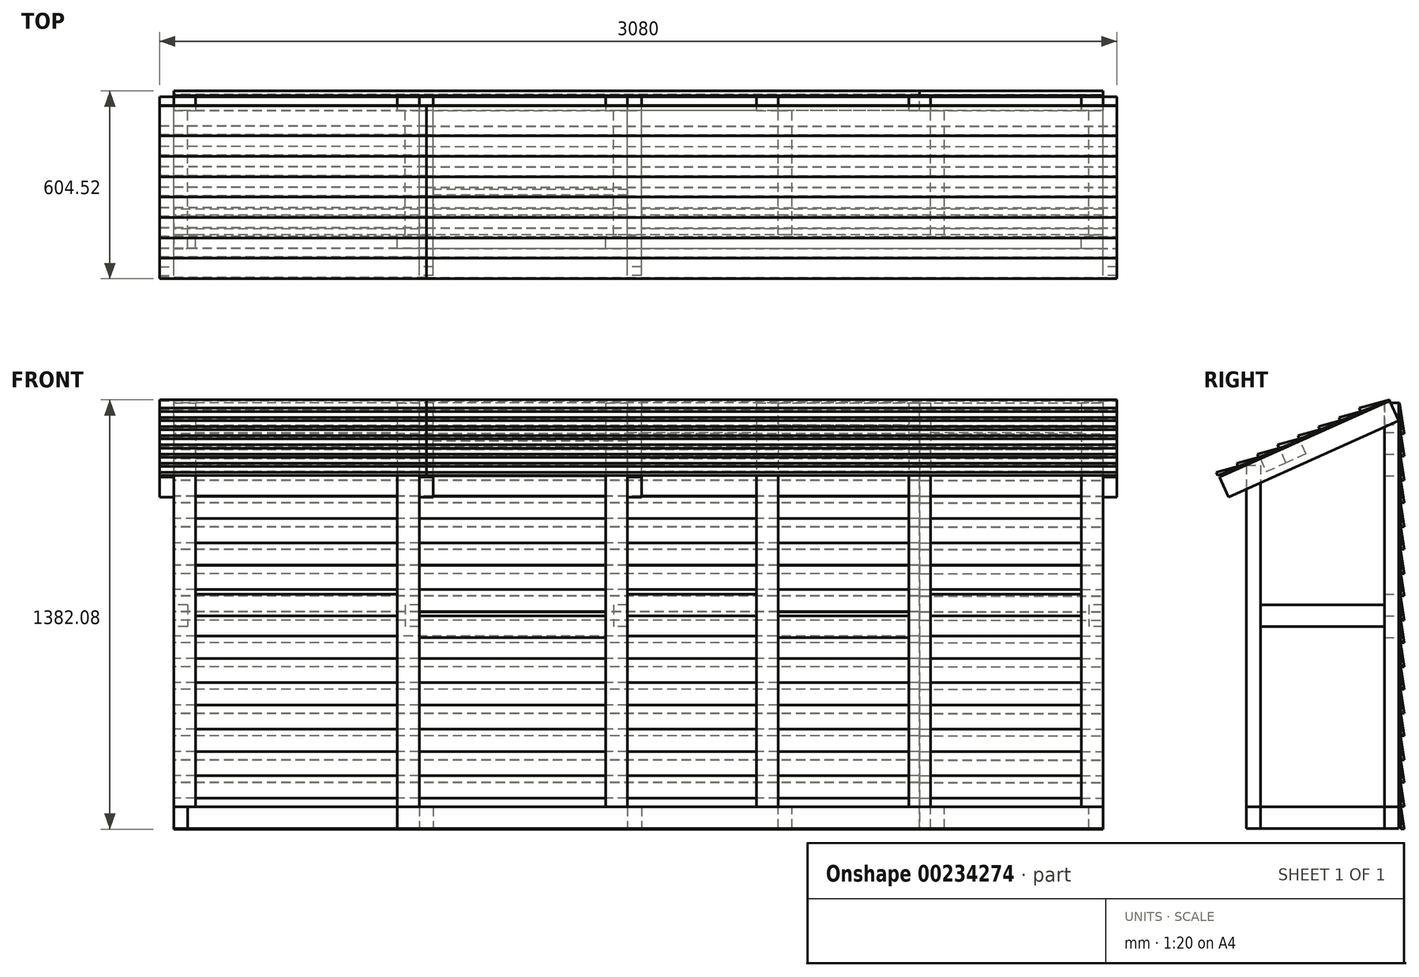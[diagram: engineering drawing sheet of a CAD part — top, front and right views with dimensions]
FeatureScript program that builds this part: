
annotation { "Feature Type Name" : "Feature", "Feature Type Description" : "" }
export const myFeature = defineFeature(function(context is Context, id is Id, definition is map)
    precondition{}
    {
        {
            var Q0;
            Q0=qCreatedBy(makeId("Top.planeOp"),FACE);
            cPlane(context, id + "F0", {"entities" : qUnion([Q0]), "cplaneType" : CPlaneType.OFFSET, "offset" : 70 * mm, "width" : 150 * mm, "height" : 150 * mm});
        }
        {
            var Q0;
            Q0=qCreatedBy(id+"F0.planeOp",FACE);
            var sketch = newSketch(context, id + "F1", { "sketchPlane" : qUnion([Q0])});
            skLineSegment(sketch, "E0.bottom", {"start": v(0, 0) * mm, "end": v(-70, 0) * mm});
            skLineSegment(sketch, "E0.top", {"start": v(0, -45) * mm, "end": v(-70, -45) * mm});
            skLineSegment(sketch, "E0.left", {"start": v(0, 0) * mm, "end": v(0, -45) * mm});
            skLineSegment(sketch, "E0.right", {"start": v(-70, 0) * mm, "end": v(-70, -45) * mm});
            skLineSegment(sketch, "E1.bottom", {"start": v(-2990, 0) * mm, "end": v(-2920, 0) * mm});
            skLineSegment(sketch, "E1.top", {"start": v(-2990, -45) * mm, "end": v(-2920, -45) * mm});
            skLineSegment(sketch, "E1.left", {"start": v(-2920, 0) * mm, "end": v(-2920, -45) * mm});
            skLineSegment(sketch, "E1.right", {"start": v(-2990, 0) * mm, "end": v(-2990, -45) * mm});
            skLineSegment(sketch, "E2.bottom", {"start": v(-2270, 0) * mm, "end": v(-2200, 0) * mm});
            skLineSegment(sketch, "E2.top", {"start": v(-2270, -45) * mm, "end": v(-2200, -45) * mm});
            skLineSegment(sketch, "E2.left", {"start": v(-2270, 0) * mm, "end": v(-2270, -45) * mm});
            skLineSegment(sketch, "E2.right", {"start": v(-2200, 0) * mm, "end": v(-2200, -45) * mm});
            skLineSegment(sketch, "E3.bottom", {"start": v(-1600, 0) * mm, "end": v(-1530, 0) * mm});
            skLineSegment(sketch, "E3.top", {"start": v(-1600, -45) * mm, "end": v(-1530, -45) * mm});
            skLineSegment(sketch, "E3.left", {"start": v(-1600, 0) * mm, "end": v(-1600, -45) * mm});
            skLineSegment(sketch, "E3.right", {"start": v(-1530, 0) * mm, "end": v(-1530, -45) * mm});
            skLineSegment(sketch, "E4.bottom", {"start": v(-1115, 0) * mm, "end": v(-1045, 0) * mm});
            skLineSegment(sketch, "E4.top", {"start": v(-1115, -45) * mm, "end": v(-1045, -45) * mm});
            skLineSegment(sketch, "E4.left", {"start": v(-1115, 0) * mm, "end": v(-1115, -45) * mm});
            skLineSegment(sketch, "E4.right", {"start": v(-1045, 0) * mm, "end": v(-1045, -45) * mm});
            skLineSegment(sketch, "E5.bottom", {"start": v(-625, 0) * mm, "end": v(-555, 0) * mm});
            skLineSegment(sketch, "E5.top", {"start": v(-625, -45) * mm, "end": v(-555, -45) * mm});
            skLineSegment(sketch, "E5.left", {"start": v(-625, 0) * mm, "end": v(-625, -45) * mm});
            skLineSegment(sketch, "E5.right", {"start": v(-555, 0) * mm, "end": v(-555, -45) * mm});
            skLineSegment(sketch, "E6.0.1.0", {"start": v(-1600, -445) * mm, "end": v(-1530, -445) * mm});
            skLineSegment(sketch, "E6.0.1.3", {"start": v(-2990, -445) * mm, "end": v(-2920, -445) * mm});
            skLineSegment(sketch, "E6.0.1.5", {"start": v(-2990, -445) * mm, "end": v(-2990, -490) * mm});
            skLineSegment(sketch, "E6.0.1.6", {"start": v(-70, -445) * mm, "end": v(-70, -490) * mm});
            skLineSegment(sketch, "E6.0.1.7", {"start": v(-2990, -490) * mm, "end": v(-2920, -490) * mm});
            skLineSegment(sketch, "E6.0.1.8", {"start": v(-2920, -445) * mm, "end": v(-2920, -490) * mm});
            skLineSegment(sketch, "E6.0.1.9", {"start": v(-2270, -490) * mm, "end": v(-2200, -490) * mm});
            skLineSegment(sketch, "E6.0.1.11", {"start": v(0, -445) * mm, "end": v(0, -490) * mm});
            skLineSegment(sketch, "E6.0.1.12", {"start": v(-1600, -490) * mm, "end": v(-1530, -490) * mm});
            skLineSegment(sketch, "E6.0.1.13", {"start": v(-1600, -445) * mm, "end": v(-1600, -490) * mm});
            skLineSegment(sketch, "E6.0.1.14", {"start": v(-1530, -445) * mm, "end": v(-1530, -490) * mm});
            skLineSegment(sketch, "E6.0.1.15", {"start": v(0, -445) * mm, "end": v(-70, -445) * mm});
            skLineSegment(sketch, "E6.0.1.16", {"start": v(0, -490) * mm, "end": v(-70, -490) * mm});
            skLineSegment(sketch, "E6.0.1.20", {"start": v(-2200, -445) * mm, "end": v(-2200, -490) * mm});
            skLineSegment(sketch, "E6.0.1.21", {"start": v(-2270, -445) * mm, "end": v(-2270, -490) * mm});
            skLineSegment(sketch, "E6.0.1.23", {"start": v(-2270, -445) * mm, "end": v(-2200, -445) * mm});
            skLineSegment(sketch, "E6.direction1", {"start": v(-2990, -45) * mm, "end": v(-2875, -45) * mm, "construction": true});
            skLineSegment(sketch, "E6.direction2", {"start": v(-2990, -45) * mm, "end": v(-2990, -490) * mm, "construction": true});
            skSolve(sketch);
        }
        {
            var Q0;
            Q0=qSketchRegion(id+"F1",true);
            extrude(context, id + "F2", {"entities" : qUnion([Q0]), "depth" : 1300 * mm});
        }
        {
            var Q0;
            Q0=makeQuery(id+"F2.opExtrude","SWEPT_FACE",FACE,{"disambiguationData":[OSD([sQuery(id+"F1.wireOp",EDGE,"E0.top")])]});
            var sketch = newSketch(context, id + "F3", { "sketchPlane" : qUnion([Q0])});
            skLineSegment(sketch, "E7.bottom", {"start": v(-2920, 0) * mm, "end": v(-2875, 0) * mm, "construction": true});
            skLineSegment(sketch, "E7.top", {"start": v(-2920, 70) * mm, "end": v(-2875, 70) * mm, "construction": true});
            skLineSegment(sketch, "E7.left", {"start": v(-2920, 0) * mm, "end": v(-2920, 70) * mm, "construction": true});
            skLineSegment(sketch, "E7.right", {"start": v(-2875, 0) * mm, "end": v(-2875, 70) * mm, "construction": true});
            skLineSegment(sketch, "E8.bottom", {"start": v(-45, 0) * mm, "end": v(0, 0) * mm});
            skLineSegment(sketch, "E8.top", {"start": v(-45, 70) * mm, "end": v(0, 70) * mm});
            skLineSegment(sketch, "E8.left", {"start": v(-45, 0) * mm, "end": v(-45, 70) * mm});
            skLineSegment(sketch, "E8.right", {"start": v(0, 0) * mm, "end": v(0, 70) * mm});
            skLineSegment(sketch, "E9.0.1.0", {"start": v(-2990, 715) * mm, "end": v(-2920, 715) * mm});
            skLineSegment(sketch, "E9.0.1.2", {"start": v(-2990, 670) * mm, "end": v(-2990, 715) * mm});
            skLineSegment(sketch, "E9.0.1.5", {"start": v(-2990, 670) * mm, "end": v(-2920, 670) * mm});
            skLineSegment(sketch, "E9.0.1.7", {"start": v(-2920, 670) * mm, "end": v(-2920, 715) * mm});
            skLineSegment(sketch, "E9.0.1.9", {"start": v(-2200, 670) * mm, "end": v(-2200, 715) * mm});
            skLineSegment(sketch, "E9.0.1.10", {"start": v(-1600, 670) * mm, "end": v(-1530, 670) * mm});
            skLineSegment(sketch, "E9.0.1.11", {"start": v(-2270, 670) * mm, "end": v(-2200, 670) * mm});
            skLineSegment(sketch, "E9.0.1.12", {"start": v(-2270, 670) * mm, "end": v(-2270, 715) * mm});
            skLineSegment(sketch, "E9.0.1.13", {"start": v(-2270, 715) * mm, "end": v(-2200, 715) * mm});
            skLineSegment(sketch, "E9.0.1.14", {"start": v(-1600, 670) * mm, "end": v(-1600, 715) * mm});
            skLineSegment(sketch, "E9.0.1.15", {"start": v(-1530, 670) * mm, "end": v(-1530, 715) * mm});
            skLineSegment(sketch, "E9.0.1.16", {"start": v(-1600, 715) * mm, "end": v(-1530, 715) * mm});
            skLineSegment(sketch, "E9.0.1.17", {"start": v(-70, 670) * mm, "end": v(-70, 715) * mm});
            skLineSegment(sketch, "E9.0.1.18", {"start": v(-70, 670) * mm, "end": v(0, 670) * mm});
            skLineSegment(sketch, "E9.0.1.19", {"start": v(0, 670) * mm, "end": v(0, 715) * mm});
            skLineSegment(sketch, "E9.0.1.20", {"start": v(-70, 715) * mm, "end": v(0, 715) * mm});
            skLineSegment(sketch, "E10.bottom", {"start": v(-2200, 70) * mm, "end": v(-2155, 70) * mm});
            skLineSegment(sketch, "E10.top", {"start": v(-2200, 0) * mm, "end": v(-2155, 0) * mm});
            skLineSegment(sketch, "E10.left", {"start": v(-2200, 70) * mm, "end": v(-2200, 0) * mm});
            skLineSegment(sketch, "E10.right", {"start": v(-2155, 70) * mm, "end": v(-2155, 0) * mm});
            skLineSegment(sketch, "E11.bottom", {"start": v(-1530, 70) * mm, "end": v(-1485, 70) * mm});
            skLineSegment(sketch, "E11.top", {"start": v(-1530, 0) * mm, "end": v(-1485, 0) * mm});
            skLineSegment(sketch, "E11.left", {"start": v(-1530, 70) * mm, "end": v(-1530, 0) * mm});
            skLineSegment(sketch, "E11.right", {"start": v(-1485, 70) * mm, "end": v(-1485, 0) * mm});
            skSolve(sketch);
        }
        {
            var Q0;
            Q0=makeQuery(id+"F3.imprint","IMPRINT",FACE,{"disambiguationData":[TD([[makeQuery(id+"F3.imprint","IMPRINT",EDGE,{"derivedFrom":sQuery(id+"F3.wireOp",EDGE,"E8.bottom")}),1.0]])]});
            var Q1;
            Q1=makeQuery(id+"F3.imprint","IMPRINT",FACE,{"disambiguationData":[TD([[makeQuery(id+"F3.imprint","IMPRINT",EDGE,{"derivedFrom":sQuery(id+"F3.wireOp",EDGE,"E11.bottom")}),-1.0]])]});
            var Q2;
            Q2=makeQuery(id+"F3.imprint","IMPRINT",FACE,{"disambiguationData":[TD([[makeQuery(id+"F3.imprint","IMPRINT",EDGE,{"derivedFrom":sQuery(id+"F3.wireOp",EDGE,"E10.bottom")}),-1.0]])]});
            var Q3;
            Q3=makeQuery(id+"F3.imprint","IMPRINT",FACE,{"disambiguationData":[TD([[makeQuery(id+"F3.imprint","IMPRINT",EDGE,{"derivedFrom":sQuery(id+"F3.wireOp",EDGE,"E7.bottom")}),1.0]])]});
            var Q4;
            Q4=makeQuery(id+"F2.opExtrude","SWEPT_FACE",FACE,{"disambiguationData":[OSD([sQuery(id+"F1.wireOp",EDGE,"E6.0.1.15")])]});
            extrude(context, id + "F4", {"entities" : qUnion([Q0, Q1, Q2, Q3]), "endBound" : BoundingType.UP_TO_SURFACE, "endBoundEntityFace" : qUnion([Q4]), "depth" : 25 * mm});
        }
        {
            var Q0;
            Q0=makeQuery(id+"F2.opExtrude","SWEPT_FACE",FACE,{"disambiguationData":[OSD([sQuery(id+"F1.wireOp",EDGE,"E1.right")])]});
            var sketch = newSketch(context, id + "F5", { "sketchPlane" : qUnion([Q0])});
            skLineSegment(sketch, "E12.0", {"start": v(45, 0) * mm, "end": v(0, 0) * mm});
            skLineSegment(sketch, "E12.1", {"start": v(45, 70) * mm, "end": v(0, 70) * mm});
            skLineSegment(sketch, "E12.3", {"start": v(0, 0) * mm, "end": v(0, 70) * mm});
            skLineSegment(sketch, "E13", {"start": v(45, 70) * mm, "end": v(45, 0) * mm});
            skSolve(sketch);
        }
        {
            var Q0;
            Q0=qSketchRegion(id+"F5",true);
            var Q1;
            Q1=makeQuery(id+"F4.opExtrude","SWEPT_FACE",FACE,{"disambiguationData":[OSD([sQuery(id+"F3.wireOp",EDGE,"E11.left")])]});
            extrude(context, id + "F6", {"entities" : qUnion([Q0]), "oppositeDirection" : true, "endBoundEntityFace" : qUnion([Q1]), "depth" : 2400 * mm});
        }
        {
            var Q0;
            Q0=makeQuery(id+"F2.opExtrude","SWEPT_FACE",FACE,{"disambiguationData":[OSD([sQuery(id+"F1.wireOp",EDGE,"E0.left")])]});
            var sketch = newSketch(context, id + "F7", { "sketchPlane" : qUnion([Q0])});
            skLineSegment(sketch, "E14.bottom", {"start": v(-45, 0) * mm, "end": v(0, 0) * mm});
            skLineSegment(sketch, "E14.top", {"start": v(-45, 70) * mm, "end": v(0, 70) * mm});
            skLineSegment(sketch, "E14.right", {"start": v(0, 0) * mm, "end": v(0, 70) * mm});
            skLineSegment(sketch, "E15", {"start": v(-45, 70) * mm, "end": v(-45, 0) * mm});
            skSolve(sketch);
        }
        {
            var Q0;
            Q0=makeQuery(id+"F2.opExtrude","SWEPT_FACE",FACE,{"disambiguationData":[OSD([sQuery(id+"F1.wireOp",EDGE,"E1.right")])]});
            var sketch = newSketch(context, id + "F8", { "sketchPlane" : qUnion([Q0])});
            skLineSegment(sketch, "E16", {"start": v(490, 1170) * mm, "end": v(490, 1370) * mm});
            skLineSegment(sketch, "E17", {"start": v(490, 1370) * mm, "end": v(445, 1370) * mm});
            skPoint(sketch, "E18", {"position": v(445, 1170) * mm});
            skLineSegment(sketch, "E19", {"start": v(445, 1170) * mm, "end": v(445, 1370) * mm});
            skLineSegment(sketch, "E20", {"start": v(445, 1170) * mm, "end": v(490, 1170) * mm});
            skSolve(sketch);
        }
        {
            var Q0;
            Q0=qSketchRegion(id+"F8",true);
            extrude(context, id + "F9", {"entities" : qUnion([Q0]), "operationType" : NewBodyOperationType.REMOVE, "endBound" : BoundingType.THROUGH_ALL, "oppositeDirection" : true, "depth" : 25 * mm});
        }
        {
            var Q0;
            Q0=makeQuery(id+"F2.opExtrude","SWEPT_FACE",FACE,{"disambiguationData":[OSD([sQuery(id+"F1.wireOp",EDGE,"E6.0.1.21")])]});
            var sketch = newSketch(context, id + "F10", { "sketchPlane" : qUnion([Q0])});
            skLineSegment(sketch, "E21.bottom", {"start": v(490, 70) * mm, "end": v(445, 70) * mm});
            skLineSegment(sketch, "E21.top", {"start": v(490, 0) * mm, "end": v(445, 0) * mm});
            skLineSegment(sketch, "E21.left", {"start": v(490, 70) * mm, "end": v(490, 0) * mm});
            skLineSegment(sketch, "E22", {"start": v(445, 70) * mm, "end": v(445, 0) * mm});
            skPoint(sketch, "E23.orphan", {"position": v(445, 0) * mm});
            skSolve(sketch);
        }
        {
            var Q0;
            Q0=qSketchRegion(id+"F10",true);
            var Q1;
            Q1=makeQuery(id+"F2.opExtrude","SWEPT_FACE",FACE,{"disambiguationData":[OSD([sQuery(id+"F1.wireOp",EDGE,"E6.0.1.11")])]});
            extrude(context, id + "F11", {"entities" : qUnion([Q0]), "endBound" : BoundingType.UP_TO_SURFACE, "oppositeDirection" : true, "endBoundEntityFace" : qUnion([Q1]), "depth" : 25 * mm});
        }
        {
            var Q0;
            Q0=makeQuery(id+"F2.opExtrude","SWEPT_FACE",FACE,{"disambiguationData":[OSD([sQuery(id+"F1.wireOp",EDGE,"E3.right")])]});
            var sketch = newSketch(context, id + "F12", { "sketchPlane" : qUnion([Q0])});
            skLineSegment(sketch, "E24.bottom", {"start": v(-45, 755) * mm, "end": v(0, 755) * mm});
            skLineSegment(sketch, "E24.top", {"start": v(-45, 685) * mm, "end": v(0, 685) * mm});
            skLineSegment(sketch, "E24.left", {"start": v(-45, 755) * mm, "end": v(-45, 685) * mm});
            skLineSegment(sketch, "E24.right", {"start": v(0, 755) * mm, "end": v(0, 685) * mm});
            skSolve(sketch);
        }
        {
            var Q0;
            Q0=qSketchRegion(id+"F12",true);
            extrude(context, id + "F13", {"entities" : qUnion([Q0]), "endBound" : BoundingType.UP_TO_NEXT, "depth" : 25 * mm});
        }
        {
            var Q0;
            Q0=makeQuery(id+"F2.opExtrude","SWEPT_FACE",FACE,{"disambiguationData":[OSD([sQuery(id+"F1.wireOp",EDGE,"E5.right")])]});
            var sketch = newSketch(context, id + "F14", { "sketchPlane" : qUnion([Q0])});
            skLineSegment(sketch, "E25.0", {"start": v(-45, 755) * mm, "end": v(0, 755) * mm});
            skLineSegment(sketch, "E25.1", {"start": v(-45, 685) * mm, "end": v(0, 685) * mm});
            skLineSegment(sketch, "E25.2", {"start": v(-45, 755) * mm, "end": v(-45, 685) * mm});
            skLineSegment(sketch, "E25.3", {"start": v(0, 755) * mm, "end": v(0, 685) * mm});
            skSolve(sketch);
        }
        {
            var Q0;
            Q0=qSketchRegion(id+"F14",true);
            extrude(context, id + "F15", {"entities" : qUnion([Q0]), "endBound" : BoundingType.UP_TO_NEXT, "depth" : 25 * mm});
        }
        {
            var Q0;
            Q0=makeQuery(id+"F2.opExtrude","SWEPT_FACE",FACE,{"disambiguationData":[OSD([sQuery(id+"F1.wireOp",EDGE,"E4.right")])]});
            var sketch = newSketch(context, id + "F16", { "sketchPlane" : qUnion([Q0])});
            skPoint(sketch, "E26.firstSnap0", {"position": v(0, 685) * mm});
            skLineSegment(sketch, "E26.bottom", {"start": v(-45, 685) * mm, "end": v(0, 685) * mm});
            skLineSegment(sketch, "E26.top", {"start": v(-45, 615) * mm, "end": v(0, 615) * mm});
            skLineSegment(sketch, "E26.left", {"start": v(-45, 685) * mm, "end": v(-45, 615) * mm});
            skLineSegment(sketch, "E26.right", {"start": v(0, 685) * mm, "end": v(0, 615) * mm});
            skSolve(sketch);
        }
        {
            var Q0;
            Q0=qSketchRegion(id+"F16",true);
            extrude(context, id + "F17", {"entities" : qUnion([Q0]), "endBound" : BoundingType.UP_TO_NEXT, "depth" : 25 * mm});
        }
        {
            var Q0;
            Q0=makeQuery(id+"F2.opExtrude","SWEPT_FACE",FACE,{"disambiguationData":[OSD([sQuery(id+"F1.wireOp",EDGE,"E3.left")])]});
            var sketch = newSketch(context, id + "F18", { "sketchPlane" : qUnion([Q0])});
            skLineSegment(sketch, "E27.top", {"start": v(45, 685) * mm, "end": v(0, 685) * mm});
            skLineSegment(sketch, "E27.left", {"start": v(45, 615) * mm, "end": v(45, 685) * mm});
            skLineSegment(sketch, "E27.right", {"start": v(0, 615) * mm, "end": v(0, 685) * mm});
            skLineSegment(sketch, "E28", {"start": v(0, 615) * mm, "end": v(45, 615) * mm});
            skSolve(sketch);
        }
        {
            var Q0;
            Q0=qSketchRegion(id+"F18",true);
            extrude(context, id + "F19", {"entities" : qUnion([Q0]), "endBound" : BoundingType.UP_TO_NEXT, "depth" : 25 * mm});
        }
        {
            var Q0;
            Q0=makeQuery(id+"F2.opExtrude","SWEPT_FACE",FACE,{"disambiguationData":[OSD([sQuery(id+"F1.wireOp",EDGE,"E2.left")])]});
            var sketch = newSketch(context, id + "F20", { "sketchPlane" : qUnion([Q0])});
            skLineSegment(sketch, "E29.0", {"start": v(45, 755) * mm, "end": v(0, 755) * mm});
            skLineSegment(sketch, "E29.1", {"start": v(45, 685) * mm, "end": v(0, 685) * mm});
            skLineSegment(sketch, "E29.2", {"start": v(45, 755) * mm, "end": v(45, 685) * mm});
            skLineSegment(sketch, "E29.3", {"start": v(0, 755) * mm, "end": v(0, 685) * mm});
            skSolve(sketch);
        }
        {
            var Q0;
            Q0=qSketchRegion(id+"F20",true);
            extrude(context, id + "F21", {"entities" : qUnion([Q0]), "endBound" : BoundingType.UP_TO_NEXT, "depth" : 25 * mm});
        }
        {
            var Q0;
            Q0=makeQuery(id+"F2.opExtrude","SWEPT_FACE",FACE,{"disambiguationData":[OSD([sQuery(id+"F1.wireOp",EDGE,"E0.left")])]});
            var sketch = newSketch(context, id + "F22", { "sketchPlane" : qUnion([Q0])});
            skLineSegment(sketch, "E30", {"start": v(-575.96, 1131.36) * mm, "end": v(-28.7, 1377.33) * mm});
            skLineSegment(sketch, "E31", {"start": v(-575.96, 1131.36) * mm, "end": v(-547.27, 1067.52) * mm});
            skLineSegment(sketch, "E32", {"start": v(-547.27, 1067.52) * mm, "end": v(0, 1313.48) * mm});
            skLineSegment(sketch, "E33", {"start": v(-28.7, 1377.33) * mm, "end": v(0, 1313.48) * mm});
            skSolve(sketch);
        }
        {
            var Q0;
            Q0=qSketchRegion(id+"F22",true);
            extrude(context, id + "F23", {"entities" : qUnion([Q0]), "depth" : 45 * mm});
        }
        {
            var Q0;
            Q0=makeQuery(id+"F2.opExtrude","SWEPT_FACE",FACE,{"disambiguationData":[OSD([sQuery(id+"F1.wireOp",EDGE,"E6.0.1.5")])]});
            var sketch = newSketch(context, id + "F24", { "sketchPlane" : qUnion([Q0])});
            skLineSegment(sketch, "E34.0", {"start": v(575.96, 1131.36) * mm, "end": v(28.7, 1377.33) * mm});
            skLineSegment(sketch, "E34.1", {"start": v(575.96, 1131.36) * mm, "end": v(547.27, 1067.52) * mm});
            skLineSegment(sketch, "E34.2", {"start": v(547.27, 1067.52) * mm, "end": v(0, 1313.48) * mm});
            skLineSegment(sketch, "E34.3", {"start": v(28.7, 1377.33) * mm, "end": v(0, 1313.48) * mm});
            skSolve(sketch);
        }
        {
            var Q0;
            Q0=qSketchRegion(id+"F24",true);
            extrude(context, id + "F25", {"entities" : qUnion([Q0]), "depth" : 45 * mm});
        }
        {
            var Q0;
            Q0=makeQuery(id+"F2.opExtrude","SWEPT_FACE",FACE,{"disambiguationData":[OSD([sQuery(id+"F1.wireOp",EDGE,"E6.0.1.14")])]});
            var sketch = newSketch(context, id + "F26", { "sketchPlane" : qUnion([Q0])});
            skLineSegment(sketch, "E35.0", {"start": v(-575.96, 1131.36) * mm, "end": v(-28.7, 1377.33) * mm});
            skLineSegment(sketch, "E35.1", {"start": v(-575.96, 1131.36) * mm, "end": v(-547.27, 1067.52) * mm});
            skLineSegment(sketch, "E35.2", {"start": v(-547.27, 1067.52) * mm, "end": v(0, 1313.48) * mm});
            skLineSegment(sketch, "E35.3", {"start": v(-28.7, 1377.33) * mm, "end": v(0, 1313.48) * mm});
            skSolve(sketch);
        }
        {
            var Q0;
            Q0=qSketchRegion(id+"F26",true);
            extrude(context, id + "F27", {"entities" : qUnion([Q0]), "depth" : 45 * mm});
        }
        {
            var Q0;
            Q0=makeQuery(id+"F2.opExtrude","SWEPT_FACE",FACE,{"disambiguationData":[OSD([sQuery(id+"F1.wireOp",EDGE,"E2.right")])]});
            var sketch = newSketch(context, id + "F28", { "sketchPlane" : qUnion([Q0])});
            skLineSegment(sketch, "E36.0", {"start": v(-575.96, 1131.36) * mm, "end": v(-28.7, 1377.33) * mm});
            skLineSegment(sketch, "E36.1", {"start": v(-575.96, 1131.36) * mm, "end": v(-547.27, 1067.52) * mm});
            skLineSegment(sketch, "E36.2", {"start": v(-547.27, 1067.52) * mm, "end": v(0, 1313.48) * mm});
            skLineSegment(sketch, "E36.3", {"start": v(-28.7, 1377.33) * mm, "end": v(0, 1313.48) * mm});
            skSolve(sketch);
        }
        {
            var Q0;
            Q0=qSketchRegion(id+"F28",true);
            extrude(context, id + "F29", {"entities" : qUnion([Q0]), "depth" : 45 * mm});
        }
        {
            var Q0;
            Q0=makeQuery(id+"F25.opExtrude","CAP_FACE",FACE,{"disambiguationData":[OSD([sQuery(id+"F24.wireOp",EDGE,"E34.0"),sQuery(id+"F24.wireOp",EDGE,"E34.1"),sQuery(id+"F24.wireOp",EDGE,"E34.2"),sQuery(id+"F24.wireOp",EDGE,"E34.3")])],"isStart":true});
            var sketch = newSketch(context, id + "F30", { "sketchPlane" : qUnion([Q0])});
            skLineSegment(sketch, "E37", {"start": v(-445, 1190.22) * mm, "end": v(-426.55, 1149.18) * mm});
            skLineSegment(sketch, "E38", {"start": v(-362.7, 1177.88) * mm, "end": v(-381.15, 1218.92) * mm});
            skLineSegment(sketch, "E39", {"start": v(-381.15, 1218.92) * mm, "end": v(-445, 1190.22) * mm});
            skLineSegment(sketch, "E40", {"start": v(-362.7, 1177.88) * mm, "end": v(-426.55, 1149.18) * mm});
            skSolve(sketch);
        }
        {
            var Q0;
            Q0=qSketchRegion(id+"F30",true);
            extrude(context, id + "F31", {"entities" : qUnion([Q0]), "endBound" : BoundingType.UP_TO_NEXT, "depth" : 25 * mm});
        }
        {
            var Q0;
            Q0=makeQuery(id+"F29.opExtrude","CAP_FACE",FACE,{"disambiguationData":[OSD([sQuery(id+"F28.wireOp",EDGE,"E36.0"),sQuery(id+"F28.wireOp",EDGE,"E36.1"),sQuery(id+"F28.wireOp",EDGE,"E36.2"),sQuery(id+"F28.wireOp",EDGE,"E36.3")])],"isStart":false});
            var sketch = newSketch(context, id + "F32", { "sketchPlane" : qUnion([Q0])});
            skLineSegment(sketch, "E41", {"start": v(-317.3, 1247.62) * mm, "end": v(-381.15, 1218.92) * mm});
            skLineSegment(sketch, "E42", {"start": v(-381.15, 1218.92) * mm, "end": v(-362.7, 1177.88) * mm});
            skLineSegment(sketch, "E43", {"start": v(-298.86, 1206.57) * mm, "end": v(-317.3, 1247.62) * mm});
            skLineSegment(sketch, "E44", {"start": v(-298.86, 1206.57) * mm, "end": v(-362.7, 1177.88) * mm});
            skSolve(sketch);
        }
        {
            var Q0;
            Q0=qSketchRegion(id+"F32",true);
            extrude(context, id + "F33", {"entities" : qUnion([Q0]), "endBound" : BoundingType.UP_TO_NEXT, "depth" : 25 * mm});
        }
        {
            var Q0;
            Q0=makeQuery(id+"F2.opExtrude","SWEPT_FACE",FACE,{"disambiguationData":[OSD([sQuery(id+"F1.wireOp",EDGE,"E0.right")])]});
            var sketch = newSketch(context, id + "F34", { "sketchPlane" : qUnion([Q0])});
            skLineSegment(sketch, "E45.bottom", {"start": v(0, 1275) * mm, "end": v(45, 1275) * mm});
            skLineSegment(sketch, "E45.top", {"start": v(0, 1205) * mm, "end": v(45, 1205) * mm});
            skLineSegment(sketch, "E45.left", {"start": v(0, 1275) * mm, "end": v(0, 1205) * mm});
            skLineSegment(sketch, "E45.right", {"start": v(45, 1275) * mm, "end": v(45, 1205) * mm});
            skLineSegment(sketch, "E46", {"start": v(0, 1240) * mm, "end": v(45, 1240) * mm, "construction": true});
            skSolve(sketch);
        }
        {
            var Q0;
            Q0=qSketchRegion(id+"F34",true);
            extrude(context, id + "F35", {"entities" : qUnion([Q0]), "endBound" : BoundingType.UP_TO_NEXT, "depth" : 25 * mm});
        }
        {
            var Q0;
            Q0=makeQuery(id+"F2.opExtrude","SWEPT_FACE",FACE,{"disambiguationData":[OSD([sQuery(id+"F1.wireOp",EDGE,"E5.left")])]});
            var sketch = newSketch(context, id + "F36", { "sketchPlane" : qUnion([Q0])});
            skLineSegment(sketch, "E47.bottom", {"start": v(0, 1370) * mm, "end": v(45, 1370) * mm});
            skLineSegment(sketch, "E47.top", {"start": v(0, 1300) * mm, "end": v(45, 1300) * mm});
            skLineSegment(sketch, "E47.left", {"start": v(0, 1370) * mm, "end": v(0, 1300) * mm});
            skLineSegment(sketch, "E47.right", {"start": v(45, 1370) * mm, "end": v(45, 1300) * mm});
            skSolve(sketch);
        }
        {
            var Q0;
            Q0=qSketchRegion(id+"F36",true);
            extrude(context, id + "F37", {"entities" : qUnion([Q0]), "endBound" : BoundingType.UP_TO_NEXT, "depth" : 25 * mm});
        }
        {
            var Q0;
            Q0=makeQuery(id+"F2.opExtrude","SWEPT_FACE",FACE,{"disambiguationData":[OSD([sQuery(id+"F1.wireOp",EDGE,"E4.left")])]});
            var sketch = newSketch(context, id + "F38", { "sketchPlane" : qUnion([Q0])});
            skLineSegment(sketch, "E48.0", {"start": v(0, 1275) * mm, "end": v(45, 1275) * mm});
            skLineSegment(sketch, "E48.1", {"start": v(0, 1205) * mm, "end": v(45, 1205) * mm});
            skLineSegment(sketch, "E48.2", {"start": v(0, 1275) * mm, "end": v(0, 1205) * mm});
            skLineSegment(sketch, "E48.3", {"start": v(45, 1275) * mm, "end": v(45, 1205) * mm});
            skSolve(sketch);
        }
        {
            var Q0;
            Q0=qSketchRegion(id+"F38",true);
            extrude(context, id + "F39", {"entities" : qUnion([Q0]), "endBound" : BoundingType.UP_TO_NEXT, "depth" : 25 * mm});
        }
        {
            var Q0;
            Q0=makeQuery(id+"F2.opExtrude","SWEPT_FACE",FACE,{"disambiguationData":[OSD([sQuery(id+"F1.wireOp",EDGE,"E3.left")])]});
            var sketch = newSketch(context, id + "F40", { "sketchPlane" : qUnion([Q0])});
            skLineSegment(sketch, "E49.bottom", {"start": v(0, 1205) * mm, "end": v(45, 1205) * mm});
            skLineSegment(sketch, "E49.top", {"start": v(0, 1135) * mm, "end": v(45, 1135) * mm});
            skLineSegment(sketch, "E49.left", {"start": v(0, 1205) * mm, "end": v(0, 1135) * mm});
            skLineSegment(sketch, "E49.right", {"start": v(45, 1205) * mm, "end": v(45, 1135) * mm});
            skSolve(sketch);
        }
        {
            var Q0;
            Q0=qSketchRegion(id+"F40",true);
            extrude(context, id + "F41", {"entities" : qUnion([Q0]), "endBound" : BoundingType.UP_TO_NEXT, "depth" : 25 * mm});
        }
        {
            var Q0;
            Q0=makeQuery(id+"F2.opExtrude","SWEPT_FACE",FACE,{"disambiguationData":[OSD([sQuery(id+"F1.wireOp",EDGE,"E2.left")])]});
            var sketch = newSketch(context, id + "F42", { "sketchPlane" : qUnion([Q0])});
            skLineSegment(sketch, "E50.bottom", {"start": v(0, 1205) * mm, "end": v(45, 1205) * mm});
            skLineSegment(sketch, "E50.top", {"start": v(0, 1275) * mm, "end": v(45, 1275) * mm});
            skLineSegment(sketch, "E50.left", {"start": v(0, 1205) * mm, "end": v(0, 1275) * mm});
            skLineSegment(sketch, "E50.right", {"start": v(45, 1205) * mm, "end": v(45, 1275) * mm});
            skSolve(sketch);
        }
        {
            var Q0;
            Q0=qSketchRegion(id+"F42",true);
            extrude(context, id + "F43", {"entities" : qUnion([Q0]), "endBound" : BoundingType.UP_TO_NEXT, "depth" : 25 * mm});
        }
        {
            var Q0;
            Q0=makeQuery(id+"F27.opExtrude","CAP_FACE",FACE,{"disambiguationData":[OSD([sQuery(id+"F26.wireOp",EDGE,"E35.0"),sQuery(id+"F26.wireOp",EDGE,"E35.1"),sQuery(id+"F26.wireOp",EDGE,"E35.2"),sQuery(id+"F26.wireOp",EDGE,"E35.3")])],"isStart":false});
            var sketch = newSketch(context, id + "F44", { "sketchPlane" : qUnion([Q0])});
            skLineSegment(sketch, "E51.0.1", {"start": v(-445, 1190.22) * mm, "end": v(-381.15, 1218.92) * mm});
            skLineSegment(sketch, "E51.0.3", {"start": v(-381.15, 1218.92) * mm, "end": v(-445, 1190.22) * mm});
            skLineSegment(sketch, "E51.1", {"start": v(-445, 1190.22) * mm, "end": v(-426.55, 1149.18) * mm});
            skLineSegment(sketch, "E51.3", {"start": v(-362.7, 1177.88) * mm, "end": v(-381.15, 1218.92) * mm});
            skLineSegment(sketch, "E51.4", {"start": v(-381.15, 1218.92) * mm, "end": v(-445, 1190.22) * mm});
            skLineSegment(sketch, "E52", {"start": v(-426.55, 1149.18) * mm, "end": v(-362.7, 1177.88) * mm});
            skSolve(sketch);
        }
        {
            var Q0;
            Q0=qSketchRegion(id+"F44",true);
            extrude(context, id + "F45", {"entities" : qUnion([Q0]), "endBound" : BoundingType.UP_TO_NEXT, "depth" : 25 * mm});
        }
        {
            var Q0;
            Q0=makeQuery(id+"F2.opExtrude","SWEPT_FACE",FACE,{"disambiguationData":[OSD([sQuery(id+"F1.wireOp",EDGE,"E1.right")])]});
            var sketch = newSketch(context, id + "F46", { "sketchPlane" : qUnion([Q0])});
            skLineSegment(sketch, "E53", {"start": v(0, 1370) * mm, "end": v(-7.26, 1270.26) * mm});
            skLineSegment(sketch, "E54", {"start": v(-7.26, 1270.26) * mm, "end": v(-18.23, 1271.06) * mm});
            skLineSegment(sketch, "E55", {"start": v(-18.23, 1271.06) * mm, "end": v(-3, 1370.22) * mm});
            skLineSegment(sketch, "E56", {"start": v(-3, 1370.22) * mm, "end": v(0, 1370) * mm});
            skLineSegment(sketch, "E57", {"start": v(-3, 1298.03) * mm, "end": v(-18.23, 1198.87) * mm});
            skLineSegment(sketch, "E58", {"start": v(-18.23, 1198.87) * mm, "end": v(-7.26, 1198.07) * mm});
            skLineSegment(sketch, "E59", {"start": v(-7.26, 1198.07) * mm, "end": v(0, 1297.8) * mm});
            skLineSegment(sketch, "E60", {"start": v(0, 1297.8) * mm, "end": v(-3, 1298.03) * mm});
            skLineSegment(sketch, "E61.0.1.0", {"start": v(-7.26, 1048.07) * mm, "end": v(0, 1147.8) * mm});
            skLineSegment(sketch, "E61.0.1.1", {"start": v(0, 1220) * mm, "end": v(-7.26, 1120.26) * mm});
            skLineSegment(sketch, "E61.0.1.2", {"start": v(-3, 1148.03) * mm, "end": v(-18.23, 1048.87) * mm});
            skLineSegment(sketch, "E61.0.1.3", {"start": v(-18.23, 1121.06) * mm, "end": v(-3, 1220.22) * mm});
            skLineSegment(sketch, "E61.0.1.4", {"start": v(-3, 1220.22) * mm, "end": v(0, 1220) * mm});
            skLineSegment(sketch, "E61.0.1.5", {"start": v(-18.23, 1048.87) * mm, "end": v(-7.26, 1048.07) * mm});
            skLineSegment(sketch, "E61.0.1.6", {"start": v(0, 1147.8) * mm, "end": v(-3, 1148.03) * mm});
            skLineSegment(sketch, "E61.0.1.7", {"start": v(-7.26, 1120.26) * mm, "end": v(-18.23, 1121.06) * mm});
            skLineSegment(sketch, "E61.0.2.0", {"start": v(-7.26, 898.07) * mm, "end": v(0, 997.8) * mm});
            skLineSegment(sketch, "E61.0.2.1", {"start": v(0, 1070) * mm, "end": v(-7.26, 970.26) * mm});
            skLineSegment(sketch, "E61.0.2.2", {"start": v(-3, 998.03) * mm, "end": v(-18.23, 898.87) * mm});
            skLineSegment(sketch, "E61.0.2.3", {"start": v(-18.23, 971.06) * mm, "end": v(-3, 1070.22) * mm});
            skLineSegment(sketch, "E61.0.2.4", {"start": v(-3, 1070.22) * mm, "end": v(0, 1070) * mm});
            skLineSegment(sketch, "E61.0.2.5", {"start": v(-18.23, 898.87) * mm, "end": v(-7.26, 898.07) * mm});
            skLineSegment(sketch, "E61.0.2.6", {"start": v(0, 997.8) * mm, "end": v(-3, 998.03) * mm});
            skLineSegment(sketch, "E61.0.2.7", {"start": v(-7.26, 970.26) * mm, "end": v(-18.23, 971.06) * mm});
            skLineSegment(sketch, "E61.0.3.0", {"start": v(-7.26, 748.07) * mm, "end": v(0, 847.8) * mm});
            skLineSegment(sketch, "E61.0.3.1", {"start": v(0, 920) * mm, "end": v(-7.26, 820.26) * mm});
            skLineSegment(sketch, "E61.0.3.2", {"start": v(-3, 848.03) * mm, "end": v(-18.23, 748.87) * mm});
            skLineSegment(sketch, "E61.0.3.3", {"start": v(-18.23, 821.06) * mm, "end": v(-3, 920.22) * mm});
            skLineSegment(sketch, "E61.0.3.4", {"start": v(-3, 920.22) * mm, "end": v(0, 920) * mm});
            skLineSegment(sketch, "E61.0.3.5", {"start": v(-18.23, 748.87) * mm, "end": v(-7.26, 748.07) * mm});
            skLineSegment(sketch, "E61.0.3.6", {"start": v(0, 847.8) * mm, "end": v(-3, 848.03) * mm});
            skLineSegment(sketch, "E61.0.3.7", {"start": v(-7.26, 820.26) * mm, "end": v(-18.23, 821.06) * mm});
            skLineSegment(sketch, "E61.0.4.0", {"start": v(-7.26, 598.07) * mm, "end": v(0, 697.8) * mm});
            skLineSegment(sketch, "E61.0.4.1", {"start": v(0, 770) * mm, "end": v(-7.26, 670.26) * mm});
            skLineSegment(sketch, "E61.0.4.2", {"start": v(-3, 698.03) * mm, "end": v(-18.23, 598.87) * mm});
            skLineSegment(sketch, "E61.0.4.3", {"start": v(-18.23, 671.06) * mm, "end": v(-3, 770.22) * mm});
            skLineSegment(sketch, "E61.0.4.4", {"start": v(-3, 770.22) * mm, "end": v(0, 770) * mm});
            skLineSegment(sketch, "E61.0.4.5", {"start": v(-18.23, 598.87) * mm, "end": v(-7.26, 598.07) * mm});
            skLineSegment(sketch, "E61.0.4.6", {"start": v(0, 697.8) * mm, "end": v(-3, 698.03) * mm});
            skLineSegment(sketch, "E61.0.4.7", {"start": v(-7.26, 670.26) * mm, "end": v(-18.23, 671.06) * mm});
            skLineSegment(sketch, "E61.direction1", {"start": v(-18.23, 1198.87) * mm, "end": v(8.8, 1198.87) * mm, "construction": true});
            skLineSegment(sketch, "E61.direction2", {"start": v(-18.23, 1198.87) * mm, "end": v(-18.23, 1048.87) * mm, "construction": true});
            skLineSegment(sketch, "E62.0.0.5", {"start": v(-7.26, 448.07) * mm, "end": v(0, 547.8) * mm});
            skLineSegment(sketch, "E62.3.0.5", {"start": v(0, 620) * mm, "end": v(-7.26, 520.26) * mm});
            skLineSegment(sketch, "E62.6.0.5", {"start": v(-3, 548.03) * mm, "end": v(-18.23, 448.87) * mm});
            skLineSegment(sketch, "E62.9.0.5", {"start": v(-18.23, 521.06) * mm, "end": v(-3, 620.22) * mm});
            skLineSegment(sketch, "E62.12.0.5", {"start": v(-3, 620.22) * mm, "end": v(0, 620) * mm});
            skLineSegment(sketch, "E62.15.0.5", {"start": v(-18.23, 448.87) * mm, "end": v(-7.26, 448.07) * mm});
            skLineSegment(sketch, "E62.18.0.5", {"start": v(0, 547.8) * mm, "end": v(-3, 548.03) * mm});
            skLineSegment(sketch, "E62.21.0.5", {"start": v(-7.26, 520.26) * mm, "end": v(-18.23, 521.06) * mm});
            skLineSegment(sketch, "E62.0.0.6", {"start": v(-7.26, 298.07) * mm, "end": v(0, 397.8) * mm});
            skLineSegment(sketch, "E62.3.0.6", {"start": v(0, 470) * mm, "end": v(-7.26, 370.26) * mm});
            skLineSegment(sketch, "E62.6.0.6", {"start": v(-3, 398.03) * mm, "end": v(-18.23, 298.87) * mm});
            skLineSegment(sketch, "E62.9.0.6", {"start": v(-18.23, 371.06) * mm, "end": v(-3, 470.22) * mm});
            skLineSegment(sketch, "E62.12.0.6", {"start": v(-3, 470.22) * mm, "end": v(0, 470) * mm});
            skLineSegment(sketch, "E62.15.0.6", {"start": v(-18.23, 298.87) * mm, "end": v(-7.26, 298.07) * mm});
            skLineSegment(sketch, "E62.18.0.6", {"start": v(0, 397.8) * mm, "end": v(-3, 398.03) * mm});
            skLineSegment(sketch, "E62.21.0.6", {"start": v(-7.26, 370.26) * mm, "end": v(-18.23, 371.06) * mm});
            skLineSegment(sketch, "E62.0.0.7", {"start": v(-7.26, 148.07) * mm, "end": v(0, 247.8) * mm});
            skLineSegment(sketch, "E62.3.0.7", {"start": v(0, 320) * mm, "end": v(-7.26, 220.26) * mm});
            skLineSegment(sketch, "E62.6.0.7", {"start": v(-3, 248.03) * mm, "end": v(-18.23, 148.87) * mm});
            skLineSegment(sketch, "E62.9.0.7", {"start": v(-18.23, 221.06) * mm, "end": v(-3, 320.22) * mm});
            skLineSegment(sketch, "E62.12.0.7", {"start": v(-3, 320.22) * mm, "end": v(0, 320) * mm});
            skLineSegment(sketch, "E62.15.0.7", {"start": v(-18.23, 148.87) * mm, "end": v(-7.26, 148.07) * mm});
            skLineSegment(sketch, "E62.18.0.7", {"start": v(0, 247.8) * mm, "end": v(-3, 248.03) * mm});
            skLineSegment(sketch, "E62.21.0.7", {"start": v(-7.26, 220.26) * mm, "end": v(-18.23, 221.06) * mm});
            skLineSegment(sketch, "E63.0.0.8", {"start": v(-7.26, -1.93) * mm, "end": v(0, 97.8) * mm});
            skLineSegment(sketch, "E63.3.0.8", {"start": v(0, 170) * mm, "end": v(-7.26, 70.26) * mm});
            skLineSegment(sketch, "E63.6.0.8", {"start": v(-3, 98.03) * mm, "end": v(-18.23, -1.13) * mm});
            skLineSegment(sketch, "E63.9.0.8", {"start": v(-18.23, 71.06) * mm, "end": v(-3, 170.22) * mm});
            skLineSegment(sketch, "E63.12.0.8", {"start": v(-3, 170.22) * mm, "end": v(0, 170) * mm});
            skLineSegment(sketch, "E63.15.0.8", {"start": v(-18.23, -1.13) * mm, "end": v(-7.26, -1.93) * mm});
            skLineSegment(sketch, "E63.18.0.8", {"start": v(0, 97.8) * mm, "end": v(-3, 98.03) * mm});
            skLineSegment(sketch, "E63.21.0.8", {"start": v(-7.26, 70.26) * mm, "end": v(-18.23, 71.06) * mm});
            skSolve(sketch);
        }
        {
            var Q0;
            Q0 = qSketchRegion(id + "F46", true);
            var Q1;
            Q1=makeQuery(id+"F2.opExtrude","SWEPT_FACE",FACE,{"disambiguationData":[OSD([sQuery(id+"F1.wireOp",EDGE,"E3.right")])]});
            extrude(context, id + "F47", {"entities" : qUnion([Q0]), "oppositeDirection" : true, "endBoundEntityFace" : qUnion([Q1]), "depth" : 2400 * mm});
        }
        {
            var Q0;
            Q0=makeQuery(id+"F6.opExtrude","SWEPT_FACE",FACE,{"disambiguationData":[OSD([sQuery(id+"F5.wireOp",EDGE,"E13")])]});
            var sketch = newSketch(context, id + "F48", { "sketchPlane" : qUnion([Q0])});
            skLineSegment(sketch, "E64.bottom", {"start": v(-2990, 0) * mm, "end": v(-2894, 0) * mm});
            skLineSegment(sketch, "E64.top", {"start": v(-2990, 70) * mm, "end": v(-2945, 70) * mm});
            skLineSegment(sketch, "E64.left", {"start": v(-2990, 0) * mm, "end": v(-2990, 70) * mm});
            skLineSegment(sketch, "E64.right", {"start": v(-2945, 0) * mm, "end": v(-2945, 70) * mm});
            skSolve(sketch);
        }
        {
            var Q0;
            Q0 = qSketchRegion(id + "F48", true);
            var Q1;
            Q1=makeQuery(id+"F2.opExtrude","SWEPT_FACE",FACE,{"disambiguationData":[OSD([sQuery(id+"F1.wireOp",EDGE,"E6.0.1.7")])]});
            extrude(context, id + "F49", {"entities" : qUnion([Q0]), "endBound" : BoundingType.UP_TO_SURFACE, "endBoundEntityFace" : qUnion([Q1]), "depth" : 25 * mm});
        }
        {
            var Q0;
            Q0 = qSketchRegion(id + "F7", true);
            var Q1;
            Q1=makeQuery(id+"F6.opExtrude","CAP_FACE",FACE,{"disambiguationData":[OSD([sQuery(id+"F5.wireOp",EDGE,"E12.0"),sQuery(id+"F5.wireOp",EDGE,"E12.1"),sQuery(id+"F5.wireOp",EDGE,"E12.3"),sQuery(id+"F5.wireOp",EDGE,"E13")])],"isStart":false});
            extrude(context, id + "F50", {"entities" : qUnion([Q0]), "endBound" : BoundingType.UP_TO_SURFACE, "oppositeDirection" : true, "endBoundEntityFace" : qUnion([Q1]), "depth" : 25 * mm});
        }
        {
            var Q0;
            Q0=makeQuery(id+"F2.opExtrude","SWEPT_FACE",FACE,{"disambiguationData":[OSD([sQuery(id+"F1.wireOp",EDGE,"E0.top")])]});
            var sketch = newSketch(context, id + "F51", { "sketchPlane" : qUnion([Q0])});
            skLineSegment(sketch, "E65.bottom", {"start": v(0, 720) * mm, "end": v(-45, 720) * mm});
            skLineSegment(sketch, "E65.top", {"start": v(0, 650) * mm, "end": v(-45, 650) * mm});
            skLineSegment(sketch, "E65.left", {"start": v(0, 720) * mm, "end": v(0, 650) * mm});
            skLineSegment(sketch, "E65.right", {"start": v(-45, 720) * mm, "end": v(-45, 650) * mm});
            skLineSegment(sketch, "E66.bottom", {"start": v(-1530, 720) * mm, "end": v(-1575, 720) * mm});
            skLineSegment(sketch, "E66.top", {"start": v(-1530, 650) * mm, "end": v(-1575, 650) * mm});
            skLineSegment(sketch, "E66.left", {"start": v(-1530, 720) * mm, "end": v(-1530, 650) * mm});
            skLineSegment(sketch, "E66.right", {"start": v(-1575, 720) * mm, "end": v(-1575, 650) * mm});
            skLineSegment(sketch, "E67.bottom", {"start": v(-2200, 720) * mm, "end": v(-2245, 720) * mm});
            skLineSegment(sketch, "E67.top", {"start": v(-2200, 650) * mm, "end": v(-2245, 650) * mm});
            skLineSegment(sketch, "E67.left", {"start": v(-2200, 720) * mm, "end": v(-2200, 650) * mm});
            skLineSegment(sketch, "E67.right", {"start": v(-2245, 720) * mm, "end": v(-2245, 650) * mm});
            skLineSegment(sketch, "E68.bottom", {"start": v(-2945, 720) * mm, "end": v(-2990, 720) * mm});
            skLineSegment(sketch, "E68.top", {"start": v(-2945, 650) * mm, "end": v(-2990, 650) * mm});
            skLineSegment(sketch, "E68.left", {"start": v(-2945, 720) * mm, "end": v(-2945, 650) * mm});
            skLineSegment(sketch, "E68.right", {"start": v(-2990, 720) * mm, "end": v(-2990, 650) * mm});
            skSolve(sketch);
        }
        {
            var Q0;
            Q0 = qSketchRegion(id + "F51", true);
            var Q1;
            Q1=makeQuery(id+"F2.opExtrude","SWEPT_FACE",FACE,{"disambiguationData":[OSD([sQuery(id+"F1.wireOp",EDGE,"E6.0.1.15")])]});
            extrude(context, id + "F52", {"entities" : qUnion([Q0]), "endBound" : BoundingType.UP_TO_SURFACE, "endBoundEntityFace" : qUnion([Q1]), "depth" : 25 * mm});
        }
        {
            var Q0;
            Q0=makeQuery(id+"F2.opExtrude","SWEPT_FACE",FACE,{"disambiguationData":[OSD([sQuery(id+"F1.wireOp",EDGE,"E0.left")])]});
            var sketch = newSketch(context, id + "F53", { "sketchPlane" : qUnion([Q0])});
            skLineSegment(sketch, "E69.0", {"start": v(0, 1370) * mm, "end": v(7.26, 1270.26) * mm});
            skLineSegment(sketch, "E69.1", {"start": v(7.26, 1270.26) * mm, "end": v(18.23, 1271.06) * mm});
            skLineSegment(sketch, "E69.2", {"start": v(18.23, 1271.06) * mm, "end": v(3, 1370.22) * mm});
            skLineSegment(sketch, "E69.3", {"start": v(3, 1370.22) * mm, "end": v(0, 1370) * mm});
            skLineSegment(sketch, "E69.4", {"start": v(3, 1298.03) * mm, "end": v(18.23, 1198.87) * mm});
            skLineSegment(sketch, "E69.5", {"start": v(18.23, 1198.87) * mm, "end": v(7.26, 1198.07) * mm});
            skLineSegment(sketch, "E69.6", {"start": v(7.26, 1198.07) * mm, "end": v(0, 1297.8) * mm});
            skLineSegment(sketch, "E69.7", {"start": v(0, 1297.8) * mm, "end": v(3, 1298.03) * mm});
            skLineSegment(sketch, "E69.8", {"start": v(7.26, 1048.07) * mm, "end": v(0, 1147.8) * mm});
            skLineSegment(sketch, "E69.9", {"start": v(0, 1220) * mm, "end": v(7.26, 1120.26) * mm});
            skLineSegment(sketch, "E69.10", {"start": v(3, 1148.03) * mm, "end": v(18.23, 1048.87) * mm});
            skLineSegment(sketch, "E69.11", {"start": v(18.23, 1121.06) * mm, "end": v(3, 1220.22) * mm});
            skLineSegment(sketch, "E69.12", {"start": v(3, 1220.22) * mm, "end": v(0, 1220) * mm});
            skLineSegment(sketch, "E69.13", {"start": v(18.23, 1048.87) * mm, "end": v(7.26, 1048.07) * mm});
            skLineSegment(sketch, "E69.14", {"start": v(0, 1147.8) * mm, "end": v(3, 1148.03) * mm});
            skLineSegment(sketch, "E69.15", {"start": v(7.26, 1120.26) * mm, "end": v(18.23, 1121.06) * mm});
            skLineSegment(sketch, "E69.16", {"start": v(7.26, 898.07) * mm, "end": v(0, 997.8) * mm});
            skLineSegment(sketch, "E69.17", {"start": v(0, 1070) * mm, "end": v(7.26, 970.26) * mm});
            skLineSegment(sketch, "E69.18", {"start": v(3, 998.03) * mm, "end": v(18.23, 898.87) * mm});
            skLineSegment(sketch, "E69.19", {"start": v(18.23, 971.06) * mm, "end": v(3, 1070.22) * mm});
            skLineSegment(sketch, "E69.20", {"start": v(3, 1070.22) * mm, "end": v(0, 1070) * mm});
            skLineSegment(sketch, "E69.21", {"start": v(18.23, 898.87) * mm, "end": v(7.26, 898.07) * mm});
            skLineSegment(sketch, "E69.22", {"start": v(0, 997.8) * mm, "end": v(3, 998.03) * mm});
            skLineSegment(sketch, "E69.23", {"start": v(7.26, 970.26) * mm, "end": v(18.23, 971.06) * mm});
            skLineSegment(sketch, "E69.24", {"start": v(7.26, 748.07) * mm, "end": v(0, 847.8) * mm});
            skLineSegment(sketch, "E69.25", {"start": v(0, 920) * mm, "end": v(7.26, 820.26) * mm});
            skLineSegment(sketch, "E69.26", {"start": v(3, 848.03) * mm, "end": v(18.23, 748.87) * mm});
            skLineSegment(sketch, "E69.27", {"start": v(18.23, 821.06) * mm, "end": v(3, 920.22) * mm});
            skLineSegment(sketch, "E69.28", {"start": v(3, 920.22) * mm, "end": v(0, 920) * mm});
            skLineSegment(sketch, "E69.29", {"start": v(18.23, 748.87) * mm, "end": v(7.26, 748.07) * mm});
            skLineSegment(sketch, "E69.30", {"start": v(0, 847.8) * mm, "end": v(3, 848.03) * mm});
            skLineSegment(sketch, "E69.31", {"start": v(7.26, 820.26) * mm, "end": v(18.23, 821.06) * mm});
            skLineSegment(sketch, "E69.32", {"start": v(7.26, 598.07) * mm, "end": v(0, 697.8) * mm});
            skLineSegment(sketch, "E69.33", {"start": v(0, 770) * mm, "end": v(7.26, 670.26) * mm});
            skLineSegment(sketch, "E69.34", {"start": v(3, 698.03) * mm, "end": v(18.23, 598.87) * mm});
            skLineSegment(sketch, "E69.35", {"start": v(18.23, 671.06) * mm, "end": v(3, 770.22) * mm});
            skLineSegment(sketch, "E69.36", {"start": v(3, 770.22) * mm, "end": v(0, 770) * mm});
            skLineSegment(sketch, "E69.37", {"start": v(18.23, 598.87) * mm, "end": v(7.26, 598.07) * mm});
            skLineSegment(sketch, "E69.38", {"start": v(0, 697.8) * mm, "end": v(3, 698.03) * mm});
            skLineSegment(sketch, "E69.39", {"start": v(7.26, 670.26) * mm, "end": v(18.23, 671.06) * mm});
            skLineSegment(sketch, "E69.42", {"start": v(7.26, 448.07) * mm, "end": v(0, 547.8) * mm});
            skLineSegment(sketch, "E69.43", {"start": v(0, 620) * mm, "end": v(7.26, 520.26) * mm});
            skLineSegment(sketch, "E69.44", {"start": v(3, 548.03) * mm, "end": v(18.23, 448.87) * mm});
            skLineSegment(sketch, "E69.45", {"start": v(18.23, 521.06) * mm, "end": v(3, 620.22) * mm});
            skLineSegment(sketch, "E69.46", {"start": v(3, 620.22) * mm, "end": v(0, 620) * mm});
            skLineSegment(sketch, "E69.47", {"start": v(18.23, 448.87) * mm, "end": v(7.26, 448.07) * mm});
            skLineSegment(sketch, "E69.48", {"start": v(0, 547.8) * mm, "end": v(3, 548.03) * mm});
            skLineSegment(sketch, "E69.49", {"start": v(7.26, 520.26) * mm, "end": v(18.23, 521.06) * mm});
            skLineSegment(sketch, "E69.50", {"start": v(7.26, 298.07) * mm, "end": v(0, 397.8) * mm});
            skLineSegment(sketch, "E69.51", {"start": v(0, 470) * mm, "end": v(7.26, 370.26) * mm});
            skLineSegment(sketch, "E69.52", {"start": v(3, 398.03) * mm, "end": v(18.23, 298.87) * mm});
            skLineSegment(sketch, "E69.53", {"start": v(18.23, 371.06) * mm, "end": v(3, 470.22) * mm});
            skLineSegment(sketch, "E69.54", {"start": v(3, 470.22) * mm, "end": v(0, 470) * mm});
            skLineSegment(sketch, "E69.55", {"start": v(18.23, 298.87) * mm, "end": v(7.26, 298.07) * mm});
            skLineSegment(sketch, "E69.56", {"start": v(0, 397.8) * mm, "end": v(3, 398.03) * mm});
            skLineSegment(sketch, "E69.57", {"start": v(7.26, 370.26) * mm, "end": v(18.23, 371.06) * mm});
            skLineSegment(sketch, "E69.58", {"start": v(7.26, 148.07) * mm, "end": v(0, 247.8) * mm});
            skLineSegment(sketch, "E69.59", {"start": v(0, 320) * mm, "end": v(7.26, 220.26) * mm});
            skLineSegment(sketch, "E69.60", {"start": v(3, 248.03) * mm, "end": v(18.23, 148.87) * mm});
            skLineSegment(sketch, "E69.61", {"start": v(18.23, 221.06) * mm, "end": v(3, 320.22) * mm});
            skLineSegment(sketch, "E69.62", {"start": v(3, 320.22) * mm, "end": v(0, 320) * mm});
            skLineSegment(sketch, "E69.63", {"start": v(18.23, 148.87) * mm, "end": v(7.26, 148.07) * mm});
            skLineSegment(sketch, "E69.64", {"start": v(0, 247.8) * mm, "end": v(3, 248.03) * mm});
            skLineSegment(sketch, "E69.65", {"start": v(7.26, 220.26) * mm, "end": v(18.23, 221.06) * mm});
            skLineSegment(sketch, "E69.66", {"start": v(7.26, -1.93) * mm, "end": v(0, 97.8) * mm});
            skLineSegment(sketch, "E69.67", {"start": v(0, 170) * mm, "end": v(7.26, 70.26) * mm});
            skLineSegment(sketch, "E69.68", {"start": v(3, 98.03) * mm, "end": v(18.23, -1.13) * mm});
            skLineSegment(sketch, "E69.69", {"start": v(18.23, 71.06) * mm, "end": v(3, 170.22) * mm});
            skLineSegment(sketch, "E69.70", {"start": v(3, 170.22) * mm, "end": v(0, 170) * mm});
            skLineSegment(sketch, "E69.71", {"start": v(18.23, -1.13) * mm, "end": v(7.26, -1.93) * mm});
            skLineSegment(sketch, "E69.72", {"start": v(0, 97.8) * mm, "end": v(3, 98.03) * mm});
            skLineSegment(sketch, "E69.73", {"start": v(7.26, 70.26) * mm, "end": v(18.23, 71.06) * mm});
            skSolve(sketch);
        }
        {
            var Q0;
            Q0 = qSketchRegion(id + "F53", true);
            var Q1;
            Q1=makeQuery(id+"F47.opExtrude","CAP_FACE",FACE,{"disambiguationData":[OSD([sQuery(id+"F46.wireOp",EDGE,"E57"),sQuery(id+"F46.wireOp",EDGE,"E58"),sQuery(id+"F46.wireOp",EDGE,"E59"),sQuery(id+"F46.wireOp",EDGE,"E60")])],"isStart":false});
            extrude(context, id + "F54", {"entities" : qUnion([Q0]), "endBound" : BoundingType.UP_TO_SURFACE, "oppositeDirection" : true, "endBoundEntityFace" : qUnion([Q1]), "depth" : 25 * mm});
        }
        {
            var Q0;
            Q0=makeQuery(id+"F23.opExtrude","SWEPT_FACE",FACE,{"disambiguationData":[OSD([sQuery(id+"F22.wireOp",EDGE,"E31")])]});
            cPlane(context, id + "F55", {"entities" : qUnion([Q0]), "cplaneType" : CPlaneType.OFFSET, "offset" : 0 * mm, "width" : 150 * mm, "height" : 150 * mm});
        }
        {
            var Q0;
            Q0=makeQuery(id+"F23.opExtrude","CAP_FACE",FACE,{"disambiguationData":[OSD([sQuery(id+"F22.wireOp",EDGE,"E30"),sQuery(id+"F22.wireOp",EDGE,"E31"),sQuery(id+"F22.wireOp",EDGE,"E32"),sQuery(id+"F22.wireOp",EDGE,"E33")])],"isStart":false});
            var sketch = newSketch(context, id + "F56", { "sketchPlane" : qUnion([Q0])});
            skLineSegment(sketch, "E70", {"start": v(-28.7, 1377.33) * mm, "end": v(-122.64, 1343.06) * mm});
            skLineSegment(sketch, "E71", {"start": v(-122.64, 1343.06) * mm, "end": v(-126.41, 1353.4) * mm});
            skLineSegment(sketch, "E72", {"start": v(-126.41, 1353.4) * mm, "end": v(-29.72, 1380.15) * mm});
            skLineSegment(sketch, "E73", {"start": v(-29.72, 1380.15) * mm, "end": v(-28.7, 1377.33) * mm});
            skLineSegment(sketch, "E74", {"start": v(-94.54, 1347.73) * mm, "end": v(-95.57, 1350.55) * mm});
            skLineSegment(sketch, "E75", {"start": v(-95.57, 1350.55) * mm, "end": v(-192.26, 1323.8) * mm});
            skLineSegment(sketch, "E76", {"start": v(-192.26, 1323.8) * mm, "end": v(-188.49, 1313.47) * mm});
            skLineSegment(sketch, "E77", {"start": v(-188.49, 1313.47) * mm, "end": v(-94.54, 1347.73) * mm});
            skLineSegment(sketch, "E78.1.0.0", {"start": v(-253.99, 1284.03) * mm, "end": v(-257.76, 1294.37) * mm});
            skLineSegment(sketch, "E78.1.0.1", {"start": v(-160.04, 1318.3) * mm, "end": v(-253.99, 1284.03) * mm});
            skLineSegment(sketch, "E78.1.0.2", {"start": v(-319.83, 1254.44) * mm, "end": v(-225.89, 1288.7) * mm});
            skLineSegment(sketch, "E78.1.0.3", {"start": v(-257.76, 1294.37) * mm, "end": v(-161.07, 1321.12) * mm});
            skLineSegment(sketch, "E78.1.0.4", {"start": v(-226.91, 1291.52) * mm, "end": v(-323.6, 1264.77) * mm});
            skLineSegment(sketch, "E78.1.0.5", {"start": v(-323.6, 1264.77) * mm, "end": v(-319.83, 1254.44) * mm});
            skLineSegment(sketch, "E78.1.0.6", {"start": v(-161.07, 1321.12) * mm, "end": v(-160.04, 1318.3) * mm});
            skLineSegment(sketch, "E78.1.0.7", {"start": v(-225.89, 1288.7) * mm, "end": v(-226.91, 1291.52) * mm});
            skLineSegment(sketch, "E78.2.0.0", {"start": v(-385.33, 1225) * mm, "end": v(-389.1, 1235.33) * mm});
            skLineSegment(sketch, "E78.2.0.1", {"start": v(-291.38, 1259.27) * mm, "end": v(-385.33, 1225) * mm});
            skLineSegment(sketch, "E78.2.0.2", {"start": v(-451.18, 1195.4) * mm, "end": v(-357.23, 1229.67) * mm});
            skLineSegment(sketch, "E78.2.0.3", {"start": v(-389.1, 1235.33) * mm, "end": v(-292.41, 1262.08) * mm});
            skLineSegment(sketch, "E78.2.0.4", {"start": v(-358.26, 1232.5) * mm, "end": v(-454.95, 1205.74) * mm});
            skLineSegment(sketch, "E78.2.0.5", {"start": v(-454.95, 1205.74) * mm, "end": v(-451.18, 1195.4) * mm});
            skLineSegment(sketch, "E78.2.0.6", {"start": v(-292.41, 1262.08) * mm, "end": v(-291.38, 1259.27) * mm});
            skLineSegment(sketch, "E78.2.0.7", {"start": v(-357.23, 1229.67) * mm, "end": v(-358.26, 1232.5) * mm});
            skLineSegment(sketch, "E78.direction1", {"start": v(-188.49, 1313.47) * mm, "end": v(-319.83, 1254.44) * mm, "construction": true});
            skLineSegment(sketch, "E79.0.3.0", {"start": v(-516.67, 1165.97) * mm, "end": v(-520.44, 1176.3) * mm});
            skLineSegment(sketch, "E79.3.3.0", {"start": v(-422.73, 1200.23) * mm, "end": v(-516.67, 1165.97) * mm});
            skLineSegment(sketch, "E79.6.3.0", {"start": v(-582.52, 1136.38) * mm, "end": v(-488.57, 1170.64) * mm});
            skLineSegment(sketch, "E79.9.3.0", {"start": v(-520.44, 1176.3) * mm, "end": v(-423.76, 1203.05) * mm});
            skLineSegment(sketch, "E79.12.3.0", {"start": v(-489.6, 1173.46) * mm, "end": v(-586.29, 1146.7) * mm});
            skLineSegment(sketch, "E79.15.3.0", {"start": v(-586.29, 1146.7) * mm, "end": v(-582.52, 1136.38) * mm});
            skLineSegment(sketch, "E79.18.3.0", {"start": v(-423.76, 1203.05) * mm, "end": v(-422.73, 1200.23) * mm});
            skLineSegment(sketch, "E79.21.3.0", {"start": v(-488.57, 1170.64) * mm, "end": v(-489.6, 1173.46) * mm});
            skSolve(sketch);
        }
        {
            var Q0;
            Q0=makeQuery(id+"F50.opExtrude","SWEPT_FACE",FACE,{"disambiguationData":[OSD([sQuery(id+"F7.wireOp",EDGE,"E15")])]});
            var sketch = newSketch(context, id + "F57", { "sketchPlane" : qUnion([Q0])});
            skLineSegment(sketch, "E80.bottom", {"start": v(-555, 70) * mm, "end": v(-510, 70) * mm});
            skLineSegment(sketch, "E80.top", {"start": v(-555, 0) * mm, "end": v(-510, 0) * mm});
            skLineSegment(sketch, "E80.left", {"start": v(-555, 70) * mm, "end": v(-555, 0) * mm});
            skLineSegment(sketch, "E80.right", {"start": v(-510, 70) * mm, "end": v(-510, 0) * mm});
            skLineSegment(sketch, "E81.bottom", {"start": v(-1045, 70) * mm, "end": v(-1000, 70) * mm});
            skLineSegment(sketch, "E81.top", {"start": v(-1045, 0) * mm, "end": v(-1000, 0) * mm});
            skLineSegment(sketch, "E81.left", {"start": v(-1045, 70) * mm, "end": v(-1045, 0) * mm});
            skLineSegment(sketch, "E81.right", {"start": v(-1000, 70) * mm, "end": v(-1000, 0) * mm});
            skSolve(sketch);
        }
        {
            var Q0;
            Q0 = qSketchRegion(id + "F57", true);
            extrude(context, id + "F58", {"entities" : qUnion([Q0]), "endBound" : BoundingType.UP_TO_NEXT, "depth" : 25 * mm});
        }
        {
            var Q0;
            Q0 = qSketchRegion(id + "F56", true);
            extrude(context, id + "F59", {"entities" : qUnion([Q0]), "oppositeDirection" : true, "depth" : 2222 * mm});
        }
        {
            var Q0;
            Q0=makeQuery(id+"F25.opExtrude","CAP_FACE",FACE,{"disambiguationData":[OSD([sQuery(id+"F24.wireOp",EDGE,"E34.0"),sQuery(id+"F24.wireOp",EDGE,"E34.1"),sQuery(id+"F24.wireOp",EDGE,"E34.2"),sQuery(id+"F24.wireOp",EDGE,"E34.3")])],"isStart":false});
            var sketch = newSketch(context, id + "F60", { "sketchPlane" : qUnion([Q0])});
            skLineSegment(sketch, "E82.2", {"start": v(45, 70) * mm, "end": v(45, 0) * mm});
            skLineSegment(sketch, "E82.3", {"start": v(45, 70) * mm, "end": v(45, 0) * mm});
            skLineSegment(sketch, "E82.6", {"start": v(45, 70) * mm, "end": v(45, 0) * mm});
            skLineSegment(sketch, "E82.7", {"start": v(45, 70) * mm, "end": v(45, 0) * mm});
            skLineSegment(sketch, "E83.0", {"start": v(28.7, 1377.33) * mm, "end": v(122.64, 1343.06) * mm});
            skLineSegment(sketch, "E83.1", {"start": v(122.64, 1343.06) * mm, "end": v(126.41, 1353.4) * mm});
            skLineSegment(sketch, "E83.2", {"start": v(126.41, 1353.4) * mm, "end": v(29.72, 1380.15) * mm});
            skLineSegment(sketch, "E83.3", {"start": v(29.72, 1380.15) * mm, "end": v(28.7, 1377.33) * mm});
            skLineSegment(sketch, "E83.4", {"start": v(94.54, 1347.73) * mm, "end": v(95.57, 1350.55) * mm});
            skLineSegment(sketch, "E83.5", {"start": v(95.57, 1350.55) * mm, "end": v(192.26, 1323.8) * mm});
            skLineSegment(sketch, "E83.6", {"start": v(192.26, 1323.8) * mm, "end": v(188.49, 1313.47) * mm});
            skLineSegment(sketch, "E83.7", {"start": v(188.49, 1313.47) * mm, "end": v(94.54, 1347.73) * mm});
            skLineSegment(sketch, "E83.8", {"start": v(253.99, 1284.03) * mm, "end": v(257.76, 1294.37) * mm});
            skLineSegment(sketch, "E83.9", {"start": v(160.04, 1318.3) * mm, "end": v(253.99, 1284.03) * mm});
            skLineSegment(sketch, "E83.10", {"start": v(319.83, 1254.44) * mm, "end": v(225.89, 1288.7) * mm});
            skLineSegment(sketch, "E83.11", {"start": v(257.76, 1294.37) * mm, "end": v(161.07, 1321.12) * mm});
            skLineSegment(sketch, "E83.12", {"start": v(226.91, 1291.52) * mm, "end": v(323.6, 1264.77) * mm});
            skLineSegment(sketch, "E83.13", {"start": v(323.6, 1264.77) * mm, "end": v(319.83, 1254.44) * mm});
            skLineSegment(sketch, "E83.14", {"start": v(161.07, 1321.12) * mm, "end": v(160.04, 1318.3) * mm});
            skLineSegment(sketch, "E83.15", {"start": v(225.89, 1288.7) * mm, "end": v(226.91, 1291.52) * mm});
            skLineSegment(sketch, "E83.16", {"start": v(385.33, 1225) * mm, "end": v(389.1, 1235.33) * mm});
            skLineSegment(sketch, "E83.17", {"start": v(291.38, 1259.27) * mm, "end": v(385.33, 1225) * mm});
            skLineSegment(sketch, "E83.18", {"start": v(451.18, 1195.4) * mm, "end": v(357.23, 1229.67) * mm});
            skLineSegment(sketch, "E83.19", {"start": v(389.1, 1235.33) * mm, "end": v(292.41, 1262.08) * mm});
            skLineSegment(sketch, "E83.20", {"start": v(358.26, 1232.5) * mm, "end": v(454.95, 1205.74) * mm});
            skLineSegment(sketch, "E83.21", {"start": v(454.95, 1205.74) * mm, "end": v(451.18, 1195.4) * mm});
            skLineSegment(sketch, "E83.22", {"start": v(292.41, 1262.08) * mm, "end": v(291.38, 1259.27) * mm});
            skLineSegment(sketch, "E83.23", {"start": v(357.23, 1229.67) * mm, "end": v(358.26, 1232.5) * mm});
            skLineSegment(sketch, "E83.24", {"start": v(188.49, 1313.47) * mm, "end": v(319.83, 1254.44) * mm});
            skLineSegment(sketch, "E83.25", {"start": v(516.67, 1165.97) * mm, "end": v(520.44, 1176.3) * mm});
            skLineSegment(sketch, "E83.26", {"start": v(422.73, 1200.23) * mm, "end": v(516.67, 1165.97) * mm});
            skLineSegment(sketch, "E83.27", {"start": v(582.52, 1136.38) * mm, "end": v(488.57, 1170.64) * mm});
            skLineSegment(sketch, "E83.28", {"start": v(520.44, 1176.3) * mm, "end": v(423.76, 1203.05) * mm});
            skLineSegment(sketch, "E83.29", {"start": v(489.6, 1173.46) * mm, "end": v(586.29, 1146.7) * mm});
            skLineSegment(sketch, "E83.30", {"start": v(586.29, 1146.7) * mm, "end": v(582.52, 1136.38) * mm});
            skLineSegment(sketch, "E83.31", {"start": v(423.76, 1203.05) * mm, "end": v(422.73, 1200.23) * mm});
            skLineSegment(sketch, "E83.32", {"start": v(488.57, 1170.64) * mm, "end": v(489.6, 1173.46) * mm});
            skSolve(sketch);
        }
        {
            var Q0;
            Q0 = qSketchRegion(id + "F60", true);
            extrude(context, id + "F61", {"entities" : qUnion([Q0]), "endBound" : BoundingType.UP_TO_NEXT, "oppositeDirection" : true, "depth" : 25 * mm});
        }
    });
